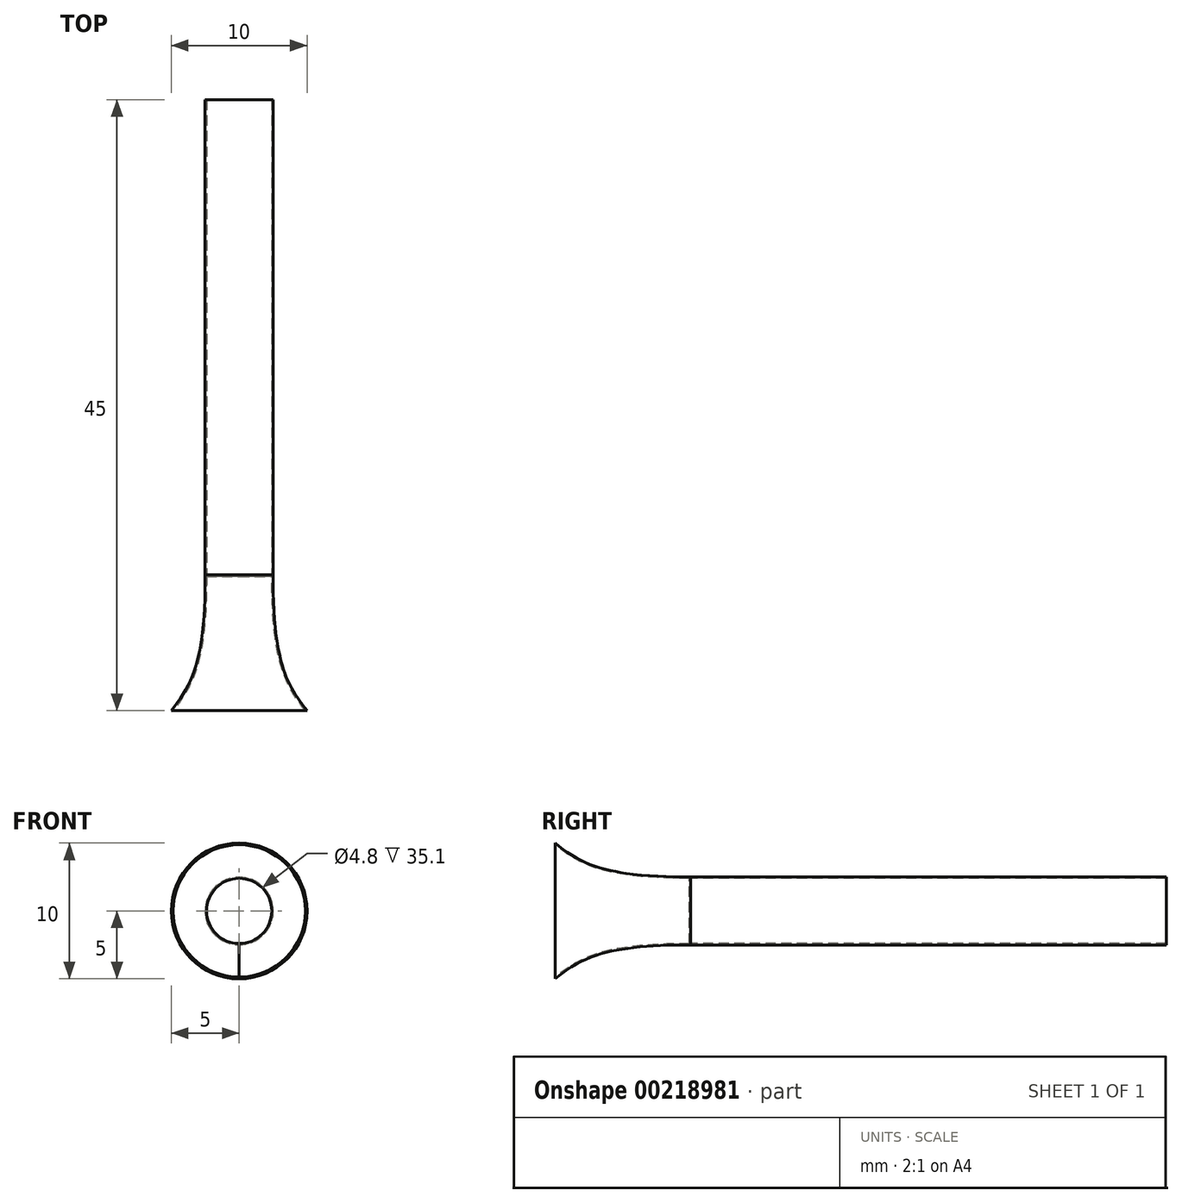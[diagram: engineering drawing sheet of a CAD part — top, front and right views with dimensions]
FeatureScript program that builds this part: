
annotation { "Feature Type Name" : "Feature", "Feature Type Description" : "" }
export const myFeature = defineFeature(function(context is Context, id is Id, definition is map)
    precondition{}
    {
        {
            var Q0;
            Q0=qCreatedBy(makeId("Right.planeOp"),FACE);
            var sketch = newSketch(context, id + "F0", { "sketchPlane" : qUnion([Q0])});
            skFitSpline(sketch, "E0", {"points": [v(0, 2.5) * mm, v(-6, 3) * mm, v(-10, 5) * mm], "startDerivative": vector(-13.96, 0) * mm, "endDerivative": vector(-9.72, 7.78) * mm});
            skLineSegment(sketch, "E1", {"start": v(-10, 5) * mm, "end": v(-10, 0) * mm});
            skLineSegment(sketch, "E2", {"start": v(-10, 0) * mm, "end": v(0, 0) * mm});
            skLineSegment(sketch, "E3", {"start": v(0, 0) * mm, "end": v(0, 2.5) * mm});
            skSolve(sketch);
        }
        {
            var Q0;
            Q0=makeQuery(id+"F0.imprint","IMPRINT",FACE,{"disambiguationData":[TD([[makeQuery(id+"F0.imprint","IMPRINT",EDGE,{"derivedFrom":sQuery(id+"F0.wireOp",EDGE,"E0")}),1.0]])]});
            var Q1;
            Q1=sQuery(id+"F0.wireOp",EDGE,"E2");
            revolve(context, id + "F1", {"entities" : qUnion([Q0]), "axis" : qUnion([Q1]), "revolveType" : RevolveType.FULL});
        }
        {
            var Q0;
            Q0=makeQuery(id+"F1.opRevolve","SWEPT_FACE",FACE,{"disambiguationData":[OSD([sQuery(id+"F0.wireOp",EDGE,"E1")])]});
            shell(context, id + "F2", {"entities" : qUnion([Q0]), "thickness" : 0.1 * mm});
        }
        {
            var Q0;
            Q0=makeQuery(id+"F2.opShell","OFFSET_FACE",FACE,{"disambiguationData":[OSD([sQuery(id+"F0.wireOp",EDGE,"E3")])]});
            extrude(context, id + "F3", {"entities" : qUnion([Q0]), "operationType" : NewBodyOperationType.REMOVE, "endBound" : BoundingType.UP_TO_NEXT, "oppositeDirection" : true, "depth" : 25 * mm});
        }
        {
            var Q0;
            Q0=qCreatedBy(makeId("Front.planeOp"),FACE);
            var sketch = newSketch(context, id + "F4", { "sketchPlane" : qUnion([Q0])});
            skCircle(sketch, "E4.0", {"center": v(0, 0) * mm, "radius": 2.5 * mm});
            skCircle(sketch, "E4.1", {"center": v(0, 0) * mm, "radius": 2.4 * mm});
            skSolve(sketch);
        }
        {
            var Q0;
            Q0=makeQuery(id+"F4.imprint","IMPRINT",FACE,{"disambiguationData":[TD([[makeQuery(id+"F4.imprint","IMPRINT",EDGE,{"derivedFrom":sQuery(id+"F4.wireOp",EDGE,"E4.0")}),1.0]])]});
            extrude(context, id + "F5", {"entities" : qUnion([Q0]), "operationType" : NewBodyOperationType.ADD, "oppositeDirection" : true, "depth" : 35 * mm});
        }
    });
